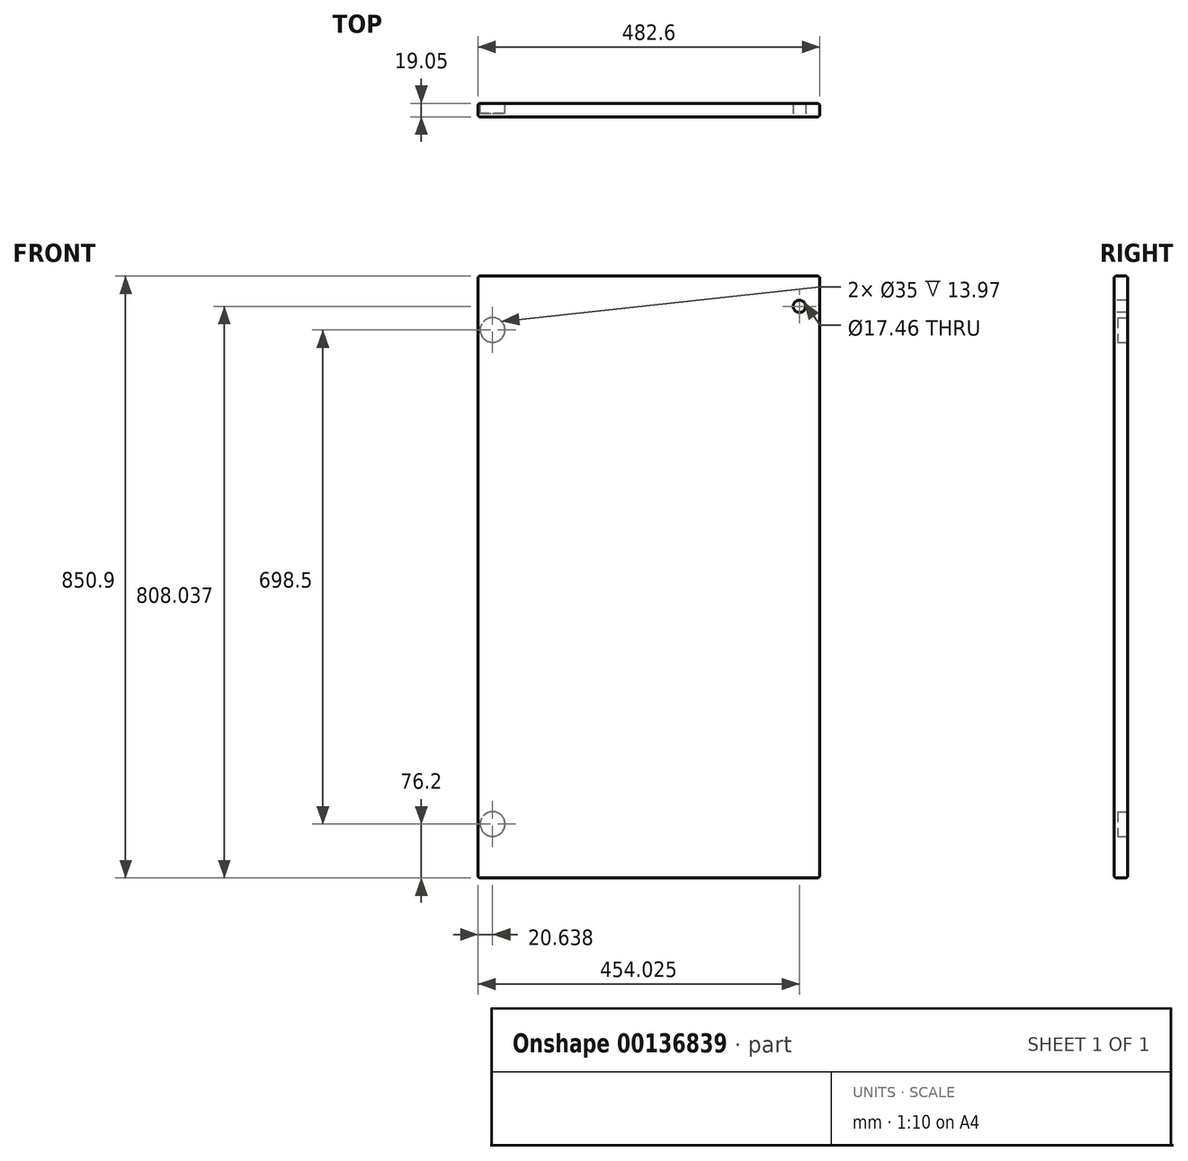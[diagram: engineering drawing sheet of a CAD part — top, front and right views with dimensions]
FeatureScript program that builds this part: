
annotation { "Feature Type Name" : "Feature", "Feature Type Description" : "" }
export const myFeature = defineFeature(function(context is Context, id is Id, definition is map)
    precondition{}
    {
        {
            var Q0;
            Q0=qCreatedBy(makeId("Front.planeOp"),FACE);
            var sketch = newSketch(context, id + "F0", { "sketchPlane" : qUnion([Q0])});
            skLineSegment(sketch, "E0.bottom", {"start": v(241.3, -425.45) * mm, "end": v(-241.3, -425.45) * mm});
            skLineSegment(sketch, "E0.top", {"start": v(241.3, 425.45) * mm, "end": v(-241.3, 425.45) * mm});
            skLineSegment(sketch, "E0.left", {"start": v(241.3, -425.45) * mm, "end": v(241.3, 425.45) * mm});
            skLineSegment(sketch, "E0.right", {"start": v(-241.3, -425.45) * mm, "end": v(-241.3, 425.45) * mm});
            skPoint(sketch, "E0.middle", {"position": v(0, 0) * mm});
            skSolve(sketch);
        }
        {
            var Q0;
            Q0=makeQuery(id+"F0.imprint","IMPRINT",FACE,{"disambiguationData":[TD([[makeQuery(id+"F0.imprint","IMPRINT",EDGE,{"derivedFrom":sQuery(id+"F0.wireOp",EDGE,"E0.bottom")}),-1.0]])]});
            extrude(context, id + "F1", {"entities" : qUnion([Q0]), "depth" : 19.05 * mm});
        }
        {
            var Q0;
            Q0=makeQuery(id+"F1.opExtrude","CAP_FACE",FACE,{"disambiguationData":[OSD([sQuery(id+"F0.wireOp",EDGE,"E0.bottom"),sQuery(id+"F0.wireOp",EDGE,"E0.top"),sQuery(id+"F0.wireOp",EDGE,"E0.left"),sQuery(id+"F0.wireOp",EDGE,"E0.right")])],"isStart":false});
            var sketch = newSketch(context, id + "F2", { "sketchPlane" : qUnion([Q0])});
            skCircle(sketch, "E1", {"center": v(212.72, 382.59) * mm, "radius": 8.73 * mm});
            skSolve(sketch);
        }
        {
            var Q0;
            Q0=makeQuery(id+"F2.imprint","IMPRINT",FACE,{"disambiguationData":[TD([[makeQuery(id+"F2.imprint","IMPRINT",EDGE,{"derivedFrom":sQuery(id+"F2.wireOp",EDGE,"E1")}),1.0]])]});
            extrude(context, id + "F3", {"entities" : qUnion([Q0]), "operationType" : NewBodyOperationType.REMOVE, "endBound" : BoundingType.THROUGH_ALL, "oppositeDirection" : true, "depth" : 25.4 * mm});
        }
        {
            var Q0;
            Q0=makeQuery(id+"F1.opExtrude","CAP_FACE",FACE,{"disambiguationData":[OSD([sQuery(id+"F0.wireOp",EDGE,"E0.bottom"),sQuery(id+"F0.wireOp",EDGE,"E0.top"),sQuery(id+"F0.wireOp",EDGE,"E0.left"),sQuery(id+"F0.wireOp",EDGE,"E0.right")])],"isStart":true});
            var sketch = newSketch(context, id + "F4", { "sketchPlane" : qUnion([Q0])});
            skCircle(sketch, "E2", {"center": v(220.66, 349.25) * mm, "radius": 17.5 * mm});
            skCircle(sketch, "E3", {"center": v(220.66, -349.25) * mm, "radius": 17.5 * mm});
            skSolve(sketch);
        }
        {
            var Q0;
            Q0=makeQuery(id+"F4.imprint","IMPRINT",FACE,{"disambiguationData":[TD([[makeQuery(id+"F4.imprint","IMPRINT",EDGE,{"derivedFrom":sQuery(id+"F4.wireOp",EDGE,"E2")}),1.0]])]});
            var Q1;
            Q1=makeQuery(id+"F4.imprint","IMPRINT",FACE,{"disambiguationData":[TD([[makeQuery(id+"F4.imprint","IMPRINT",EDGE,{"derivedFrom":sQuery(id+"F4.wireOp",EDGE,"E3")}),1.0]])]});
            extrude(context, id + "F5", {"entities" : qUnion([Q0, Q1]), "operationType" : NewBodyOperationType.REMOVE, "oppositeDirection" : true, "depth" : 13.97 * mm});
        }
        {
            var Q0;
            Q0=makeQuery(id+"F1.opExtrude","CAP_EDGE",EDGE,{"disambiguationData":[OSD([sQuery(id+"F0.wireOp",EDGE,"E0.top")])],"isStart":false});
            var Q1;
            Q1=makeQuery(id+"F1.opExtrude","CAP_EDGE",EDGE,{"disambiguationData":[OSD([sQuery(id+"F0.wireOp",EDGE,"E0.right")])],"isStart":false});
            var Q2;
            Q2=makeQuery(id+"F1.opExtrude","CAP_EDGE",EDGE,{"disambiguationData":[OSD([sQuery(id+"F0.wireOp",EDGE,"E0.bottom")])],"isStart":false});
            var Q3;
            Q3=makeQuery(id+"F1.opExtrude","CAP_EDGE",EDGE,{"disambiguationData":[OSD([sQuery(id+"F0.wireOp",EDGE,"E0.left")])],"isStart":false});
            var Q4;
            Q4=makeQuery(id+"F1.opExtrude","CAP_EDGE",EDGE,{"disambiguationData":[OSD([sQuery(id+"F0.wireOp",EDGE,"E0.top")])],"isStart":true});
            var Q5;
            Q5=makeQuery(id+"F1.opExtrude","CAP_EDGE",EDGE,{"disambiguationData":[OSD([sQuery(id+"F0.wireOp",EDGE,"E0.left")])],"isStart":true});
            var Q6;
            Q6=makeQuery(id+"F1.opExtrude","CAP_EDGE",EDGE,{"disambiguationData":[OSD([sQuery(id+"F0.wireOp",EDGE,"E0.bottom")])],"isStart":true});
            var Q7;
            Q7=makeQuery(id+"F1.opExtrude","CAP_EDGE",EDGE,{"disambiguationData":[OSD([sQuery(id+"F0.wireOp",EDGE,"E0.right")])],"isStart":true});
            var Q8;
            Q8=makeQuery(id+"F1.opExtrude","SWEPT_EDGE",EDGE,{"disambiguationData":[OSD([sQuery(id+"F0.wireOp",EDGE,"E0.top"),sQuery(id+"F0.wireOp",EDGE,"E0.right")])]});
            var Q9;
            Q9=makeQuery(id+"F1.opExtrude","SWEPT_EDGE",EDGE,{"disambiguationData":[OSD([sQuery(id+"F0.wireOp",EDGE,"E0.top"),sQuery(id+"F0.wireOp",EDGE,"E0.left")])]});
            var Q10;
            Q10=makeQuery(id+"F1.opExtrude","SWEPT_EDGE",EDGE,{"disambiguationData":[OSD([sQuery(id+"F0.wireOp",EDGE,"E0.bottom"),sQuery(id+"F0.wireOp",EDGE,"E0.left")])]});
            var Q11;
            Q11=makeQuery(id+"F1.opExtrude","SWEPT_EDGE",EDGE,{"disambiguationData":[OSD([sQuery(id+"F0.wireOp",EDGE,"E0.bottom"),sQuery(id+"F0.wireOp",EDGE,"E0.right")])]});
            fillet(context, id + "F6", {"entities" : qUnion([Q0, Q1, Q2, Q3, Q4, Q5, Q6, Q7, Q8, Q9, Q10, Q11]), "radius" : 3.17 * mm, "tangentPropagation" : true, "allowEdgeOverflow" : false});
        }
    });
